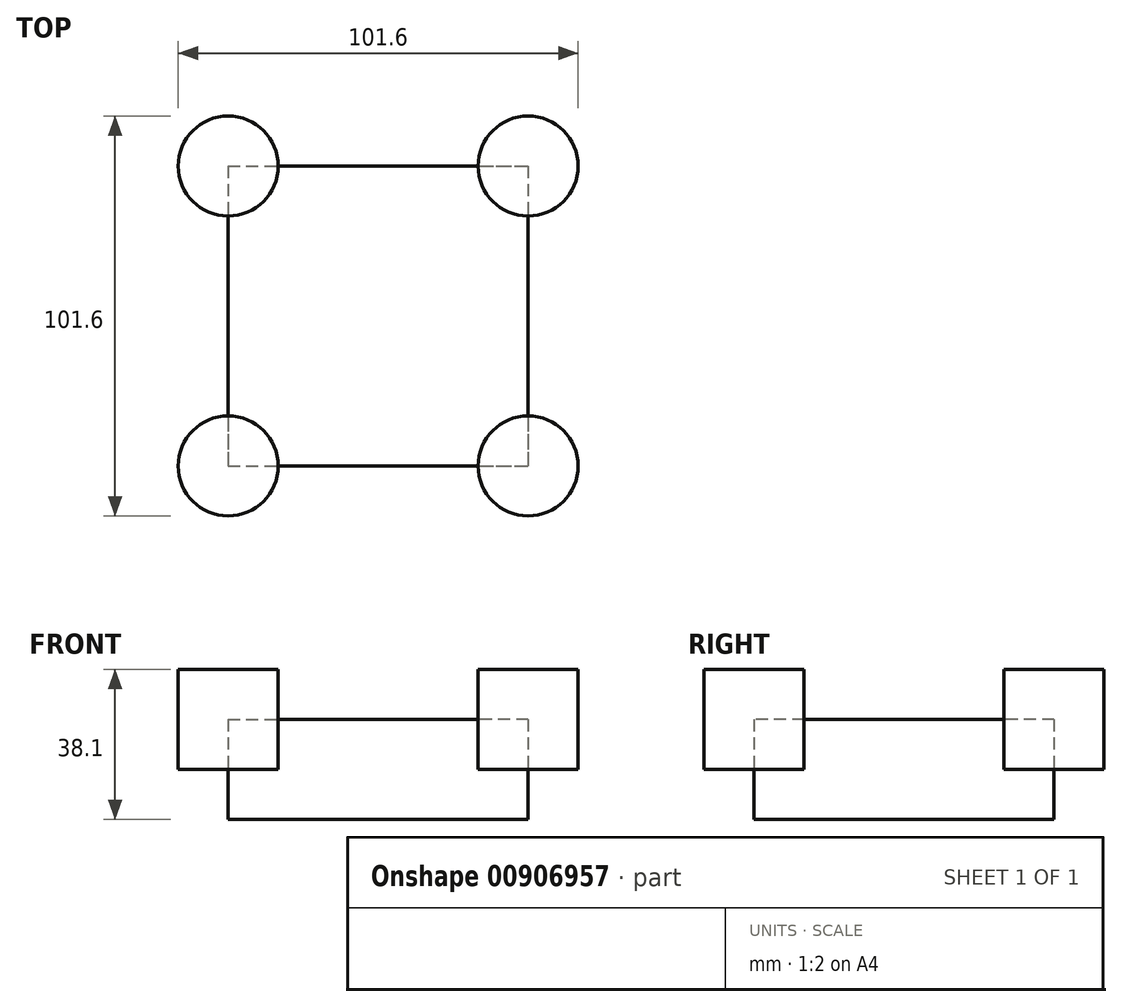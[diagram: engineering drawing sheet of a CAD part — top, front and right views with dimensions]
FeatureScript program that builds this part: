
annotation { "Feature Type Name" : "Feature", "Feature Type Description" : "" }
export const myFeature = defineFeature(function(context is Context, id is Id, definition is map)
    precondition{}
    {
        {
            var Q0;
            Q0=qCreatedBy(makeId("Top.planeOp"),FACE);
            var sketch = newSketch(context, id + "F0", { "sketchPlane" : qUnion([Q0])});
            skLineSegment(sketch, "E0.bottom", {"start": v(-38.1, 38.1) * mm, "end": v(38.1, 38.1) * mm});
            skLineSegment(sketch, "E0.top", {"start": v(-38.1, -38.1) * mm, "end": v(38.1, -38.1) * mm});
            skLineSegment(sketch, "E0.left", {"start": v(-38.1, 38.1) * mm, "end": v(-38.1, -38.1) * mm});
            skLineSegment(sketch, "E0.right", {"start": v(38.1, 38.1) * mm, "end": v(38.1, -38.1) * mm});
            skLineSegment(sketch, "E1", {"start": v(-38.1, 0) * mm, "end": v(38.1, 0) * mm, "construction": true});
            skSolve(sketch);
        }
        {
            var Q0;
            Q0=makeQuery(id+"F0.imprint","IMPRINT",FACE,{"disambiguationData":[TD([[makeQuery(id+"F0.imprint","IMPRINT",EDGE,{"derivedFrom":sQuery(id+"F0.wireOp",EDGE,"E0.bottom")}),-1.0]])]});
            extrude(context, id + "F1", {"entities" : qUnion([Q0]), "depth" : 25.4 * mm, "offsetDistance" : 25.4 * mm});
        }
        {
            var Q0;
            Q0=makeQuery(id+"F1.opExtrude","CAP_FACE",FACE,{"disambiguationData":[OSD([sQuery(id+"F0.wireOp",EDGE,"E0.bottom"),sQuery(id+"F0.wireOp",EDGE,"E0.top"),sQuery(id+"F0.wireOp",EDGE,"E0.left"),sQuery(id+"F0.wireOp",EDGE,"E0.right")])],"isStart":false});
            var sketch = newSketch(context, id + "F2", { "sketchPlane" : qUnion([Q0])});
            skCircle(sketch, "E2", {"center": v(-38.1, 38.1) * mm, "radius": 12.7 * mm});
            skLineSegment(sketch, "E3", {"start": v(0, 38.1) * mm, "end": v(0, -38.1) * mm, "construction": true});
            skLineSegment(sketch, "E4", {"start": v(-38.1, 0) * mm, "end": v(38.1, 0) * mm, "construction": true});
            skLineSegment(sketch, "E5.MirrorCS", {"start": v(38.1, 0) * mm, "end": v(-38.1, 0) * mm, "construction": true});
            skCircle(sketch, "E6.MirrorC", {"center": v(38.1, 38.1) * mm, "radius": 12.7 * mm});
            skCircle(sketch, "E7.MirrorC", {"center": v(-38.1, -38.1) * mm, "radius": 12.7 * mm});
            skCircle(sketch, "E8.MirrorC", {"center": v(38.1, -38.1) * mm, "radius": 12.7 * mm});
            skSolve(sketch);
        }
        {
            var Q0;
            Q0 = qSketchRegion(id + "F2", true);
            extrude(context, id + "F3", {"entities" : qUnion([Q0]), "operationType" : NewBodyOperationType.ADD, "endBound" : BoundingType.SYMMETRIC, "depth" : 25.4 * mm, "offsetDistance" : 25.4 * mm});
        }
    });
